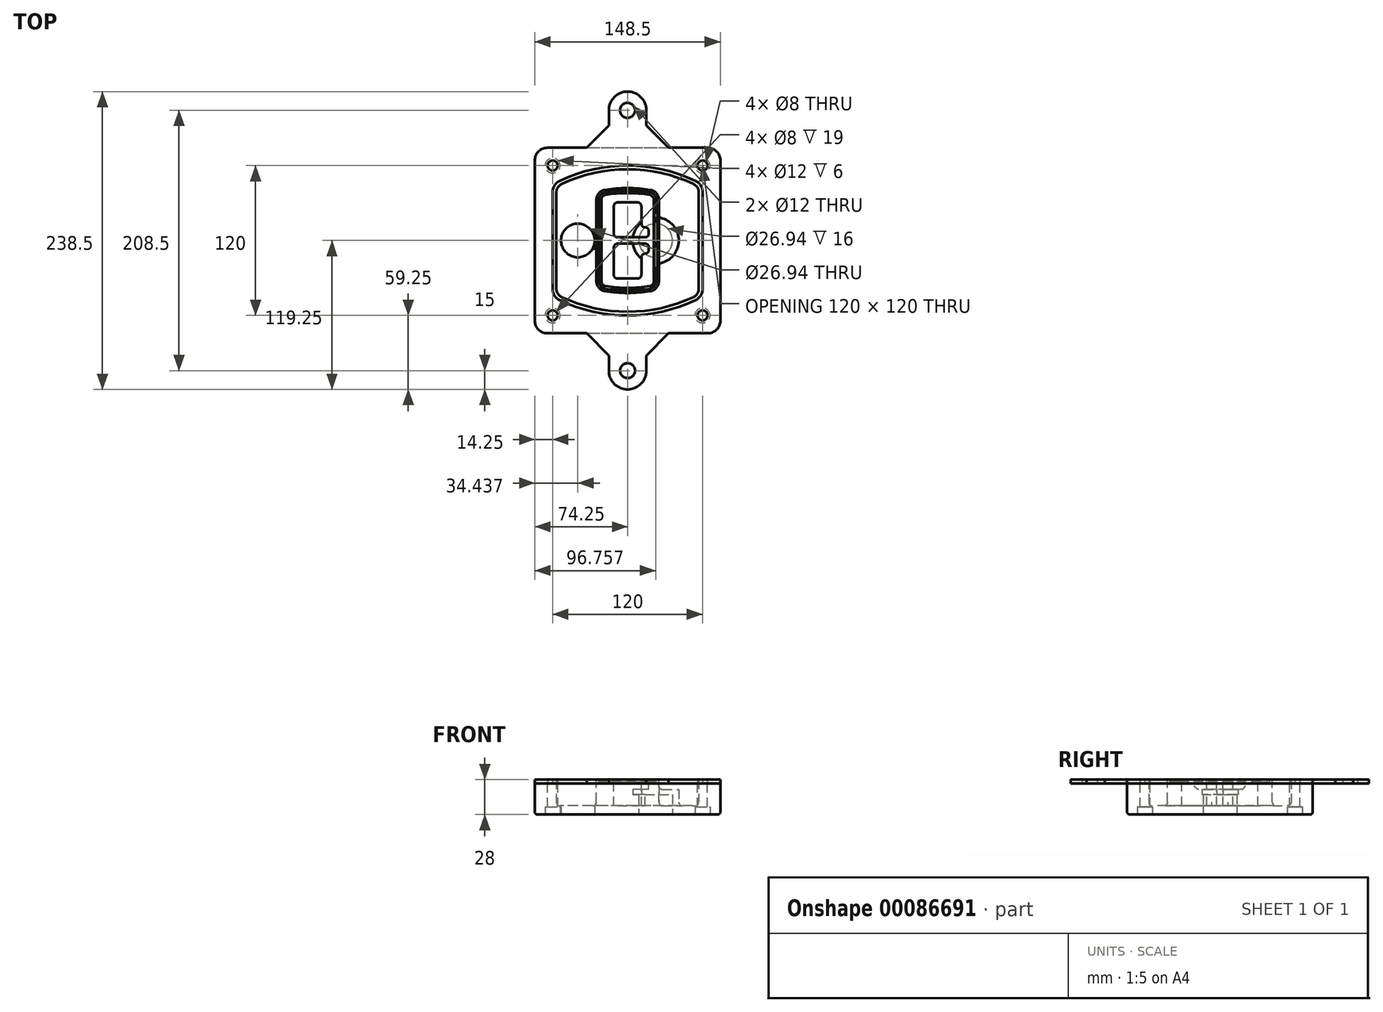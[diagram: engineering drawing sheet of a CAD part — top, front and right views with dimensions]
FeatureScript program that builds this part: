
annotation { "Feature Type Name" : "Feature", "Feature Type Description" : "" }
export const myFeature = defineFeature(function(context is Context, id is Id, definition is map)
    precondition{}
    {
        {
            var Q0;
            Q0=qCreatedBy(makeId("Top.planeOp"),FACE);
            var sketch = newSketch(context, id + "F0", { "sketchPlane" : qUnion([Q0])});
            skPoint(sketch, "E0.rect.middle", {"position": v(0, 0) * mm});
            skLineSegment(sketch, "E1.bottom", {"start": v(-64.25, -74.25) * mm, "end": v(64.25, -74.25) * mm});
            skLineSegment(sketch, "E1.top", {"start": v(-64.25, 74.25) * mm, "end": v(64.25, 74.25) * mm});
            skLineSegment(sketch, "E1.left", {"start": v(-74.25, -64.25) * mm, "end": v(-74.25, 64.25) * mm});
            skLineSegment(sketch, "E1.right", {"start": v(74.25, -64.25) * mm, "end": v(74.25, 64.25) * mm});
            skLineSegment(sketch, "E2", {"start": v(-74.25, 74.25) * mm, "end": v(74.25, -74.25) * mm, "construction": true});
            skLineSegment(sketch, "E3", {"start": v(74.25, 74.25) * mm, "end": v(-74.25, -74.25) * mm, "construction": true});
            skCircle(sketch, "E4", {"center": v(-60, 60) * mm, "radius": 4 * mm});
            skCircle(sketch, "E5", {"center": v(60, 60) * mm, "radius": 4 * mm});
            skCircle(sketch, "E6", {"center": v(60, -60) * mm, "radius": 4 * mm});
            skCircle(sketch, "E7", {"center": v(-60, -60) * mm, "radius": 4 * mm});
            skLineSegment(sketch, "E8", {"start": v(-60, 60) * mm, "end": v(60, 60) * mm, "construction": true});
            skLineSegment(sketch, "E9", {"start": v(60, 60) * mm, "end": v(60, -60) * mm, "construction": true});
            skLineSegment(sketch, "E10", {"start": v(60, -60) * mm, "end": v(-60, -60) * mm, "construction": true});
            skLineSegment(sketch, "E11", {"start": v(-60, -60) * mm, "end": v(-60, 60) * mm, "construction": true});
            skLineSegment(sketch, "E12", {"start": v(-60, 38.83) * mm, "end": v(-60, -38.83) * mm});
            skLineSegment(sketch, "E13", {"start": v(60, 38.83) * mm, "end": v(60, -38.83) * mm});
            skArc(sketch, "E14", {"start": v(54.26, 47.88) * mm, "mid": v(0, 60) * mm, "end": v(-54.26, 47.88) * mm});
            skArc(sketch, "E15", {"start": v(-54.26, -47.88) * mm, "mid": v(0, -60) * mm, "end": v(54.26, -47.88) * mm});
            skLineSegment(sketch, "E16", {"start": v(-60, 0) * mm, "end": v(60, 0) * mm, "construction": true});
            skPoint(sketch, "E17.visualSharp", {"position": v(-60, -45) * mm});
            skArc(sketch, "E17.filletArc", {"start": v(-60, -38.83) * mm, "mid": v(-58.44, -44.2) * mm, "end": v(-54.26, -47.88) * mm});
            skPoint(sketch, "E18.visualSharp", {"position": v(-60, 45) * mm});
            skArc(sketch, "E18.filletArc", {"start": v(-54.26, 47.88) * mm, "mid": v(-58.44, 44.2) * mm, "end": v(-60, 38.83) * mm});
            skPoint(sketch, "E19.visualSharp", {"position": v(60, 45) * mm});
            skArc(sketch, "E19.filletArc", {"start": v(60, 38.83) * mm, "mid": v(58.44, 44.2) * mm, "end": v(54.26, 47.88) * mm});
            skPoint(sketch, "E20.visualSharp", {"position": v(60, -45) * mm});
            skArc(sketch, "E20.filletArc", {"start": v(54.26, -47.88) * mm, "mid": v(58.44, -44.2) * mm, "end": v(60, -38.83) * mm});
            skPoint(sketch, "E21.visualSharp", {"position": v(-74.25, 74.25) * mm});
            skArc(sketch, "E21.filletArc", {"start": v(-64.25, 74.25) * mm, "mid": v(-71.32, 71.32) * mm, "end": v(-74.25, 64.25) * mm});
            skPoint(sketch, "E22.visualSharp", {"position": v(74.25, 74.25) * mm});
            skArc(sketch, "E22.filletArc", {"start": v(74.25, 64.25) * mm, "mid": v(71.32, 71.32) * mm, "end": v(64.25, 74.25) * mm});
            skPoint(sketch, "E23.visualSharp", {"position": v(74.25, -74.25) * mm});
            skArc(sketch, "E23.filletArc", {"start": v(64.25, -74.25) * mm, "mid": v(71.32, -71.32) * mm, "end": v(74.25, -64.25) * mm});
            skPoint(sketch, "E24.visualSharp", {"position": v(-74.25, -74.25) * mm});
            skArc(sketch, "E24.filletArc", {"start": v(-74.25, -64.25) * mm, "mid": v(-71.32, -71.32) * mm, "end": v(-64.25, -74.25) * mm});
            skArc(sketch, "E25.0", {"start": v(57, 38.83) * mm, "mid": v(55.9, 42.58) * mm, "end": v(52.98, 45.17) * mm});
            skLineSegment(sketch, "E25.1", {"start": v(57, 38.83) * mm, "end": v(57, -38.83) * mm});
            skArc(sketch, "E25.2", {"start": v(52.98, -45.17) * mm, "mid": v(55.9, -42.58) * mm, "end": v(57, -38.83) * mm});
            skArc(sketch, "E25.3", {"start": v(-52.98, -45.17) * mm, "mid": v(0, -57) * mm, "end": v(52.98, -45.17) * mm});
            skArc(sketch, "E25.4", {"start": v(-57, -38.83) * mm, "mid": v(-55.9, -42.58) * mm, "end": v(-52.98, -45.17) * mm});
            skArc(sketch, "E25.5", {"start": v(52.98, 45.17) * mm, "mid": v(0, 57) * mm, "end": v(-52.98, 45.17) * mm});
            skLineSegment(sketch, "E25.6", {"start": v(-57, 38.83) * mm, "end": v(-57, -38.83) * mm});
            skArc(sketch, "E25.7", {"start": v(-52.98, 45.17) * mm, "mid": v(-55.9, 42.58) * mm, "end": v(-57, 38.83) * mm});
            skArc(sketch, "E26.0", {"start": v(-55.96, 51.5) * mm, "mid": v(-61.82, 46.33) * mm, "end": v(-64, 38.83) * mm});
            skArc(sketch, "E26.1", {"start": v(55.96, 51.5) * mm, "mid": v(0, 64) * mm, "end": v(-55.96, 51.5) * mm});
            skArc(sketch, "E26.2", {"start": v(64, 38.83) * mm, "mid": v(61.82, 46.33) * mm, "end": v(55.96, 51.5) * mm});
            skLineSegment(sketch, "E26.3", {"start": v(64, 38.83) * mm, "end": v(64, -38.83) * mm});
            skArc(sketch, "E26.4", {"start": v(55.96, -51.5) * mm, "mid": v(61.82, -46.33) * mm, "end": v(64, -38.83) * mm});
            skLineSegment(sketch, "E26.5", {"start": v(-64, 38.83) * mm, "end": v(-64, -38.83) * mm});
            skArc(sketch, "E26.6", {"start": v(-55.96, -51.5) * mm, "mid": v(0, -64) * mm, "end": v(55.96, -51.5) * mm});
            skArc(sketch, "E26.7", {"start": v(-64, -38.83) * mm, "mid": v(-61.82, -46.33) * mm, "end": v(-55.96, -51.5) * mm});
            skSolve(sketch);
        }
        {
            var Q0;
            Q0=makeQuery(id+"F0.imprint","IMPRINT",FACE,{"disambiguationData":[TD([[makeQuery(id+"F0.imprint","IMPRINT",EDGE,{"derivedFrom":sQuery(id+"F0.wireOp",EDGE,"E1.bottom")}),1.0]])]});
            var Q1;
            Q1=makeQuery(id+"F0.imprint","IMPRINT",FACE,{"disambiguationData":[TD([[makeQuery(id+"F0.imprint","IMPRINT",EDGE,{"derivedFrom":sQuery(id+"F0.wireOp",EDGE,"E12")}),1.0]])]});
            var Q2;
            Q2=makeQuery(id+"F0.imprint","IMPRINT",FACE,{"disambiguationData":[TD([[makeQuery(id+"F0.imprint","IMPRINT",EDGE,{"derivedFrom":sQuery(id+"F0.wireOp",EDGE,"E25.0")}),1.0]])]});
            var Q3;
            Q3=makeQuery(id+"F0.imprint","IMPRINT",FACE,{"disambiguationData":[TD([[makeQuery(id+"F0.imprint","IMPRINT",EDGE,{"derivedFrom":sQuery(id+"F0.wireOp",EDGE,"E12")}),-1.0]])]});
            extrude(context, id + "F1", {"entities" : qUnion([Q0, Q1, Q2, Q3]), "oppositeDirection" : true, "depth" : 25 * mm});
        }
        {
            var Q0;
            Q0=makeQuery(id+"F0.imprint","IMPRINT",FACE,{"disambiguationData":[TD([[makeQuery(id+"F0.imprint","IMPRINT",EDGE,{"derivedFrom":sQuery(id+"F0.wireOp",EDGE,"E12")}),1.0]])]});
            extrude(context, id + "F2", {"entities" : qUnion([Q0]), "operationType" : NewBodyOperationType.ADD, "depth" : 3 * mm});
        }
        {
            var Q0;
            Q0=makeQuery(id+"F0.imprint","IMPRINT",FACE,{"disambiguationData":[TD([[makeQuery(id+"F0.imprint","IMPRINT",EDGE,{"derivedFrom":sQuery(id+"F0.wireOp",EDGE,"E25.0")}),1.0]])]});
            extrude(context, id + "F3", {"entities" : qUnion([Q0]), "operationType" : NewBodyOperationType.REMOVE, "oppositeDirection" : true, "depth" : 18 * mm});
        }
        {
            var Q0;
            Q0=makeQuery(id+"F2.opExtrude","CAP_FACE",FACE,{"disambiguationData":[OSD([sQuery(id+"F0.wireOp",EDGE,"E12"),sQuery(id+"F0.wireOp",EDGE,"E13"),sQuery(id+"F0.wireOp",EDGE,"E14"),sQuery(id+"F0.wireOp",EDGE,"E15"),sQuery(id+"F0.wireOp",EDGE,"E17.filletArc"),sQuery(id+"F0.wireOp",EDGE,"E18.filletArc"),sQuery(id+"F0.wireOp",EDGE,"E19.filletArc"),sQuery(id+"F0.wireOp",EDGE,"E20.filletArc"),sQuery(id+"F0.wireOp",EDGE,"E25.0"),sQuery(id+"F0.wireOp",EDGE,"E25.1"),sQuery(id+"F0.wireOp",EDGE,"E25.2"),sQuery(id+"F0.wireOp",EDGE,"E25.3"),sQuery(id+"F0.wireOp",EDGE,"E25.4"),sQuery(id+"F0.wireOp",EDGE,"E25.5"),sQuery(id+"F0.wireOp",EDGE,"E25.6"),sQuery(id+"F0.wireOp",EDGE,"E25.7")])],"isStart":false});
            var sketch = newSketch(context, id + "F4", { "sketchPlane" : qUnion([Q0])});
            skArc(sketch, "E27.0", {"start": v(-18.34, -40.45) * mm, "mid": v(0, -42) * mm, "end": v(18.34, -40.45) * mm});
            skArc(sketch, "E28.0", {"start": v(18.34, 40.45) * mm, "mid": v(0, 42) * mm, "end": v(-18.34, 40.45) * mm});
            skLineSegment(sketch, "E29", {"start": v(-25, 32.57) * mm, "end": v(-25, -32.57) * mm});
            skLineSegment(sketch, "E30", {"start": v(25, 32.57) * mm, "end": v(25, -32.57) * mm});
            skLineSegment(sketch, "E31", {"start": v(-25, 39.1) * mm, "end": v(25, 39.1) * mm, "construction": true});
            skLineSegment(sketch, "E32", {"start": v(-25, -39.1) * mm, "end": v(25, -39.1) * mm, "construction": true});
            skPoint(sketch, "E33.visualSharp", {"position": v(-25, 39.1) * mm});
            skArc(sketch, "E33.filletArc", {"start": v(-18.34, 40.45) * mm, "mid": v(-23.11, 37.73) * mm, "end": v(-25, 32.57) * mm});
            skPoint(sketch, "E34.visualSharp", {"position": v(25, 39.1) * mm});
            skArc(sketch, "E34.filletArc", {"start": v(25, 32.57) * mm, "mid": v(23.11, 37.73) * mm, "end": v(18.34, 40.45) * mm});
            skPoint(sketch, "E35.visualSharp", {"position": v(25, -39.1) * mm});
            skArc(sketch, "E35.filletArc", {"start": v(18.34, -40.45) * mm, "mid": v(23.11, -37.73) * mm, "end": v(25, -32.57) * mm});
            skPoint(sketch, "E36.visualSharp", {"position": v(-25, -39.1) * mm});
            skArc(sketch, "E36.filletArc", {"start": v(-25, -32.57) * mm, "mid": v(-23.11, -37.73) * mm, "end": v(-18.34, -40.45) * mm});
            skArc(sketch, "E37.0", {"start": v(52.98, 45.17) * mm, "mid": v(0, 57) * mm, "end": v(-52.98, 45.17) * mm});
            skArc(sketch, "E37.1", {"start": v(-52.98, 45.17) * mm, "mid": v(-55.9, 42.58) * mm, "end": v(-57, 38.83) * mm});
            skLineSegment(sketch, "E37.2", {"start": v(-57, 38.83) * mm, "end": v(-57, -38.83) * mm});
            skArc(sketch, "E37.3", {"start": v(-57, -38.83) * mm, "mid": v(-55.9, -42.58) * mm, "end": v(-52.98, -45.17) * mm});
            skArc(sketch, "E37.4", {"start": v(-52.98, -45.17) * mm, "mid": v(0, -57) * mm, "end": v(52.98, -45.17) * mm});
            skArc(sketch, "E37.5", {"start": v(52.98, -45.17) * mm, "mid": v(55.9, -42.58) * mm, "end": v(57, -38.83) * mm});
            skLineSegment(sketch, "E37.6", {"start": v(57, 38.83) * mm, "end": v(57, -38.83) * mm});
            skArc(sketch, "E37.7", {"start": v(57, 38.83) * mm, "mid": v(55.9, 42.58) * mm, "end": v(52.98, 45.17) * mm});
            skLineSegment(sketch, "E38.0", {"start": v(23, 32.57) * mm, "end": v(23, -32.57) * mm});
            skArc(sketch, "E38.1", {"start": v(18, -38.48) * mm, "mid": v(21.58, -36.44) * mm, "end": v(23, -32.57) * mm});
            skArc(sketch, "E38.2", {"start": v(-18, -38.48) * mm, "mid": v(0, -40) * mm, "end": v(18, -38.48) * mm});
            skArc(sketch, "E38.3", {"start": v(-23, -32.57) * mm, "mid": v(-21.58, -36.44) * mm, "end": v(-18, -38.48) * mm});
            skLineSegment(sketch, "E38.4", {"start": v(-23, 32.57) * mm, "end": v(-23, -32.57) * mm});
            skArc(sketch, "E38.5", {"start": v(23, 32.57) * mm, "mid": v(21.58, 36.44) * mm, "end": v(18, 38.48) * mm});
            skArc(sketch, "E38.6", {"start": v(-18, 38.48) * mm, "mid": v(-21.58, 36.44) * mm, "end": v(-23, 32.57) * mm});
            skArc(sketch, "E38.7", {"start": v(18, 38.48) * mm, "mid": v(0, 40) * mm, "end": v(-18, 38.48) * mm});
            skArc(sketch, "E39.0", {"start": v(21, 32.57) * mm, "mid": v(20.06, 35.15) * mm, "end": v(17.67, 36.5) * mm});
            skLineSegment(sketch, "E39.1", {"start": v(21, 32.57) * mm, "end": v(21, -32.57) * mm});
            skArc(sketch, "E39.2", {"start": v(17.67, -36.5) * mm, "mid": v(20.06, -35.15) * mm, "end": v(21, -32.57) * mm});
            skArc(sketch, "E39.3", {"start": v(-17.67, -36.5) * mm, "mid": v(0, -38) * mm, "end": v(17.67, -36.5) * mm});
            skArc(sketch, "E39.4", {"start": v(-21, -32.57) * mm, "mid": v(-20.06, -35.15) * mm, "end": v(-17.67, -36.5) * mm});
            skArc(sketch, "E39.5", {"start": v(17.67, 36.5) * mm, "mid": v(0, 38) * mm, "end": v(-17.67, 36.5) * mm});
            skLineSegment(sketch, "E39.6", {"start": v(-21, 32.57) * mm, "end": v(-21, -32.57) * mm});
            skArc(sketch, "E39.7", {"start": v(-17.67, 36.5) * mm, "mid": v(-20.06, 35.15) * mm, "end": v(-21, 32.57) * mm});
            skLineSegment(sketch, "E40", {"start": v(-25, 0) * mm, "end": v(25, 0) * mm, "construction": true});
            skLineSegment(sketch, "E41", {"start": v(-11, 5.5) * mm, "end": v(-11, 27.5) * mm});
            skLineSegment(sketch, "E42", {"start": v(-8, 30.5) * mm, "end": v(8, 30.5) * mm});
            skLineSegment(sketch, "E43", {"start": v(11, 27.5) * mm, "end": v(11, 13.5) * mm});
            skLineSegment(sketch, "E44", {"start": v(14, 10.5) * mm, "end": v(14, 10.5) * mm});
            skLineSegment(sketch, "E45", {"start": v(17, 7.5) * mm, "end": v(17, 5.5) * mm});
            skLineSegment(sketch, "E46", {"start": v(14, 2.5) * mm, "end": v(-8, 2.5) * mm});
            skPoint(sketch, "E47.visualSharp", {"position": v(-11, 30.5) * mm});
            skArc(sketch, "E47.filletArc", {"start": v(-8, 30.5) * mm, "mid": v(-10.12, 29.62) * mm, "end": v(-11, 27.5) * mm});
            skPoint(sketch, "E48.visualSharp", {"position": v(11, 30.5) * mm});
            skArc(sketch, "E48.filletArc", {"start": v(11, 27.5) * mm, "mid": v(10.12, 29.62) * mm, "end": v(8, 30.5) * mm});
            skPoint(sketch, "E49.visualSharp", {"position": v(11, 10.5) * mm});
            skArc(sketch, "E49.filletArc", {"start": v(11, 13.5) * mm, "mid": v(11.88, 11.38) * mm, "end": v(14, 10.5) * mm});
            skPoint(sketch, "E50.visualSharp", {"position": v(17, 10.5) * mm});
            skArc(sketch, "E50.filletArc", {"start": v(17, 7.5) * mm, "mid": v(16.12, 9.62) * mm, "end": v(14, 10.5) * mm});
            skPoint(sketch, "E51.visualSharp", {"position": v(17, 2.5) * mm});
            skArc(sketch, "E51.filletArc", {"start": v(14, 2.5) * mm, "mid": v(16.12, 3.38) * mm, "end": v(17, 5.5) * mm});
            skPoint(sketch, "E52.visualSharp", {"position": v(-11, 2.5) * mm});
            skArc(sketch, "E52.filletArc", {"start": v(-11, 5.5) * mm, "mid": v(-10.12, 3.38) * mm, "end": v(-8, 2.5) * mm});
            skLineSegment(sketch, "E53.0.MirrorCS", {"start": v(14, -2.5) * mm, "end": v(-8, -2.5) * mm});
            skArc(sketch, "E54.0.MirrorCS", {"start": v(-11, -5.5) * mm, "mid": v(-10.12, -3.38) * mm, "end": v(-8, -2.5) * mm});
            skLineSegment(sketch, "E55.0.MirrorCS", {"start": v(-11, -5.5) * mm, "end": v(-11, -27.5) * mm});
            skArc(sketch, "E56.0.MirrorCS", {"start": v(-8, -30.5) * mm, "mid": v(-10.12, -29.62) * mm, "end": v(-11, -27.5) * mm});
            skLineSegment(sketch, "E57.0.MirrorCS", {"start": v(-8, -30.5) * mm, "end": v(8, -30.5) * mm});
            skArc(sketch, "E58.0.MirrorCS", {"start": v(11, -27.5) * mm, "mid": v(10.12, -29.62) * mm, "end": v(8, -30.5) * mm});
            skLineSegment(sketch, "E59.0.MirrorCS", {"start": v(11, -27.5) * mm, "end": v(11, -13.5) * mm});
            skArc(sketch, "E60.0.MirrorCS", {"start": v(11, -13.5) * mm, "mid": v(11.88, -11.38) * mm, "end": v(14, -10.5) * mm});
            skArc(sketch, "E61.0.MirrorCS", {"start": v(17, -7.5) * mm, "mid": v(16.12, -9.62) * mm, "end": v(14, -10.5) * mm});
            skLineSegment(sketch, "E62.0.MirrorCS", {"start": v(17, -7.5) * mm, "end": v(17, -5.5) * mm});
            skArc(sketch, "E63.0.MirrorCS", {"start": v(14, -2.5) * mm, "mid": v(16.12, -3.38) * mm, "end": v(17, -5.5) * mm});
            skSolve(sketch);
        }
        {
            var Q0;
            Q0=makeQuery(id+"F4.imprint","IMPRINT",FACE,{"disambiguationData":[TD([[makeQuery(id+"F4.imprint","IMPRINT",EDGE,{"derivedFrom":sQuery(id+"F4.wireOp",EDGE,"E27.0")}),1.0]])]});
            var Q1;
            Q1=makeQuery(id+"F4.imprint","IMPRINT",FACE,{"disambiguationData":[TD([[makeQuery(id+"F4.imprint","IMPRINT",EDGE,{"derivedFrom":sQuery(id+"F4.wireOp",EDGE,"E38.0")}),-1.0]])]});
            var Q2;
            Q2=makeQuery(id+"F4.imprint","IMPRINT",FACE,{"disambiguationData":[TD([[makeQuery(id+"F4.imprint","IMPRINT",EDGE,{"derivedFrom":sQuery(id+"F4.wireOp",EDGE,"E39.0")}),1.0]])]});
            extrude(context, id + "F5", {"entities" : qUnion([Q0, Q1, Q2]), "operationType" : NewBodyOperationType.ADD, "endBound" : BoundingType.UP_TO_NEXT, "oppositeDirection" : true, "depth" : 25 * mm});
        }
        {
            var Q0;
            Q0=makeQuery(id+"F4.imprint","IMPRINT",FACE,{"disambiguationData":[TD([[makeQuery(id+"F4.imprint","IMPRINT",EDGE,{"derivedFrom":sQuery(id+"F4.wireOp",EDGE,"E38.0")}),-1.0]])]});
            extrude(context, id + "F6", {"entities" : qUnion([Q0]), "operationType" : NewBodyOperationType.REMOVE, "oppositeDirection" : true, "depth" : 2 * mm});
        }
        {
            var Q0;
            Q0=makeQuery(id+"F1.opExtrude","CAP_FACE",FACE,{"disambiguationData":[OSD([sQuery(id+"F0.wireOp",EDGE,"E1.bottom"),sQuery(id+"F0.wireOp",EDGE,"E1.top"),sQuery(id+"F0.wireOp",EDGE,"E1.left"),sQuery(id+"F0.wireOp",EDGE,"E1.right"),sQuery(id+"F0.wireOp",EDGE,"E4"),sQuery(id+"F0.wireOp",EDGE,"E5"),sQuery(id+"F0.wireOp",EDGE,"E6"),sQuery(id+"F0.wireOp",EDGE,"E7"),sQuery(id+"F0.wireOp",EDGE,"E21.filletArc"),sQuery(id+"F0.wireOp",EDGE,"E22.filletArc"),sQuery(id+"F0.wireOp",EDGE,"E23.filletArc"),sQuery(id+"F0.wireOp",EDGE,"E24.filletArc")])],"isStart":false});
            var sketch = newSketch(context, id + "F7", { "sketchPlane" : qUnion([Q0])});
            skCircle(sketch, "E64", {"center": v(22.5, 0) * mm, "radius": 13.47 * mm});
            skCircle(sketch, "E65", {"center": v(-39.81, 0) * mm, "radius": 13.47 * mm});
            skLineSegment(sketch, "E66", {"start": v(74.25, 0) * mm, "end": v(-74.25, 0) * mm});
            skCircle(sketch, "E67", {"center": v(22.5, 0) * mm, "radius": 18.47 * mm});
            skCircle(sketch, "E68", {"center": v(60, -60) * mm, "radius": 6 * mm});
            skCircle(sketch, "E69", {"center": v(-60, -60) * mm, "radius": 6 * mm});
            skCircle(sketch, "E70", {"center": v(-60, 60) * mm, "radius": 6 * mm});
            skCircle(sketch, "E71", {"center": v(60, 60) * mm, "radius": 6 * mm});
            skSolve(sketch);
        }
        {
            var Q0;
            {var subQ1=sQuery(id+"F7.wireOp",EDGE,"E66");var subQ4=sQuery(id+"F7.wireOp",EDGE,"E64");var subQ6=makeQuery(id+"F7.imprint","INTERSECT",VERTEX,{"disambiguationData":[OD(0.0)],"derivedFrom":[subQ4,subQ1]});Q0=makeQuery(id+"F7.imprint","IMPRINT",FACE,{"disambiguationData":[TD([[makeQuery(id+"F7.imprint","IMPRINT",EDGE,{"disambiguationData":[TD([[subQ6,-1.0]])],"derivedFrom":subQ4}),-1.0]])]});}
            var Q1;
            {var subQ0=sQuery(id+"F7.wireOp",EDGE,"E66");var subQ1=sQuery(id+"F7.wireOp",EDGE,"E64");var subQ3=makeQuery(id+"F7.imprint","INTERSECT",VERTEX,{"disambiguationData":[OD(0.0)],"derivedFrom":[subQ1,subQ0]});Q1=makeQuery(id+"F7.imprint","IMPRINT",FACE,{"disambiguationData":[TD([[makeQuery(id+"F7.imprint","IMPRINT",EDGE,{"disambiguationData":[TD([[subQ3,-1.0]])],"derivedFrom":subQ1}),1.0]])]});}
            var Q2;
            {var subQ0=sQuery(id+"F7.wireOp",EDGE,"E66");var subQ1=sQuery(id+"F7.wireOp",EDGE,"E64");var subQ3=makeQuery(id+"F7.imprint","INTERSECT",VERTEX,{"disambiguationData":[OD(0.0)],"derivedFrom":[subQ1,subQ0]});Q2=makeQuery(id+"F7.imprint","IMPRINT",FACE,{"disambiguationData":[TD([[makeQuery(id+"F7.imprint","IMPRINT",EDGE,{"disambiguationData":[TD([[subQ3,1.0]])],"derivedFrom":subQ1}),1.0]])]});}
            var Q3;
            {var subQ1=sQuery(id+"F7.wireOp",EDGE,"E66");var subQ4=sQuery(id+"F7.wireOp",EDGE,"E64");var subQ6=makeQuery(id+"F7.imprint","INTERSECT",VERTEX,{"disambiguationData":[OD(0.0)],"derivedFrom":[subQ4,subQ1]});Q3=makeQuery(id+"F7.imprint","IMPRINT",FACE,{"disambiguationData":[TD([[makeQuery(id+"F7.imprint","IMPRINT",EDGE,{"disambiguationData":[TD([[subQ6,1.0]])],"derivedFrom":subQ4}),-1.0]])]});}
            extrude(context, id + "F8", {"entities" : qUnion([Q0, Q1, Q2, Q3]), "operationType" : NewBodyOperationType.ADD, "oppositeDirection" : true, "depth" : 20 * mm});
        }
        {
            var Q0;
            {var subQ0=sQuery(id+"F7.wireOp",EDGE,"E66");var subQ1=sQuery(id+"F7.wireOp",EDGE,"E64");var subQ3=makeQuery(id+"F7.imprint","INTERSECT",VERTEX,{"disambiguationData":[OD(0.0)],"derivedFrom":[subQ1,subQ0]});Q0=makeQuery(id+"F7.imprint","IMPRINT",FACE,{"disambiguationData":[TD([[makeQuery(id+"F7.imprint","IMPRINT",EDGE,{"disambiguationData":[TD([[subQ3,-1.0]])],"derivedFrom":subQ1}),1.0]])]});}
            var Q1;
            {var subQ0=sQuery(id+"F7.wireOp",EDGE,"E66");var subQ1=sQuery(id+"F7.wireOp",EDGE,"E64");var subQ3=makeQuery(id+"F7.imprint","INTERSECT",VERTEX,{"disambiguationData":[OD(0.0)],"derivedFrom":[subQ1,subQ0]});Q1=makeQuery(id+"F7.imprint","IMPRINT",FACE,{"disambiguationData":[TD([[makeQuery(id+"F7.imprint","IMPRINT",EDGE,{"disambiguationData":[TD([[subQ3,1.0]])],"derivedFrom":subQ1}),1.0]])]});}
            extrude(context, id + "F9", {"entities" : qUnion([Q0, Q1]), "operationType" : NewBodyOperationType.REMOVE, "oppositeDirection" : true, "depth" : 16 * mm});
        }
        {
            var Q0;
            {var subQ0=sQuery(id+"F7.wireOp",EDGE,"E66");var subQ1=sQuery(id+"F7.wireOp",EDGE,"E65");var subQ3=makeQuery(id+"F7.imprint","INTERSECT",VERTEX,{"disambiguationData":[OD(0.0)],"derivedFrom":[subQ1,subQ0]});Q0=makeQuery(id+"F7.imprint","IMPRINT",FACE,{"disambiguationData":[TD([[makeQuery(id+"F7.imprint","IMPRINT",EDGE,{"disambiguationData":[TD([[subQ3,-1.0]])],"derivedFrom":subQ1}),1.0]])]});}
            var Q1;
            {var subQ0=sQuery(id+"F7.wireOp",EDGE,"E66");var subQ1=sQuery(id+"F7.wireOp",EDGE,"E65");var subQ3=makeQuery(id+"F7.imprint","INTERSECT",VERTEX,{"disambiguationData":[OD(0.0)],"derivedFrom":[subQ1,subQ0]});Q1=makeQuery(id+"F7.imprint","IMPRINT",FACE,{"disambiguationData":[TD([[makeQuery(id+"F7.imprint","IMPRINT",EDGE,{"disambiguationData":[TD([[subQ3,1.0]])],"derivedFrom":subQ1}),1.0]])]});}
            extrude(context, id + "F10", {"entities" : qUnion([Q0, Q1]), "operationType" : NewBodyOperationType.REMOVE, "oppositeDirection" : true, "depth" : 25 * mm});
        }
        {
            var Q0;
            Q0=makeQuery(id+"F7.imprint","IMPRINT",FACE,{"disambiguationData":[TD([[makeQuery(id+"F7.imprint","IMPRINT",EDGE,{"derivedFrom":sQuery(id+"F7.wireOp",EDGE,"E68")}),1.0]])]});
            var Q1;
            Q1=makeQuery(id+"F7.imprint","IMPRINT",FACE,{"disambiguationData":[TD([[makeQuery(id+"F7.imprint","IMPRINT",EDGE,{"derivedFrom":makeQuery(id+"F1.opExtrude","CAP_EDGE",EDGE,{"disambiguationData":[OSD([sQuery(id+"F0.wireOp",EDGE,"E5")])],"isStart":false})}),-1.0]])]});
            var Q2;
            Q2=makeQuery(id+"F7.imprint","IMPRINT",FACE,{"disambiguationData":[TD([[makeQuery(id+"F7.imprint","IMPRINT",EDGE,{"derivedFrom":sQuery(id+"F7.wireOp",EDGE,"E69")}),1.0]])]});
            var Q3;
            Q3=makeQuery(id+"F7.imprint","IMPRINT",FACE,{"disambiguationData":[TD([[makeQuery(id+"F7.imprint","IMPRINT",EDGE,{"derivedFrom":makeQuery(id+"F1.opExtrude","CAP_EDGE",EDGE,{"disambiguationData":[OSD([sQuery(id+"F0.wireOp",EDGE,"E4")])],"isStart":false})}),-1.0]])]});
            var Q4;
            Q4=makeQuery(id+"F7.imprint","IMPRINT",FACE,{"disambiguationData":[TD([[makeQuery(id+"F7.imprint","IMPRINT",EDGE,{"derivedFrom":sQuery(id+"F7.wireOp",EDGE,"E70")}),1.0]])]});
            var Q5;
            Q5=makeQuery(id+"F7.imprint","IMPRINT",FACE,{"disambiguationData":[TD([[makeQuery(id+"F7.imprint","IMPRINT",EDGE,{"derivedFrom":makeQuery(id+"F1.opExtrude","CAP_EDGE",EDGE,{"disambiguationData":[OSD([sQuery(id+"F0.wireOp",EDGE,"E7")])],"isStart":false})}),-1.0]])]});
            var Q6;
            Q6=makeQuery(id+"F7.imprint","IMPRINT",FACE,{"disambiguationData":[TD([[makeQuery(id+"F7.imprint","IMPRINT",EDGE,{"derivedFrom":sQuery(id+"F7.wireOp",EDGE,"E71")}),1.0]])]});
            var Q7;
            Q7=makeQuery(id+"F7.imprint","IMPRINT",FACE,{"disambiguationData":[TD([[makeQuery(id+"F7.imprint","IMPRINT",EDGE,{"derivedFrom":makeQuery(id+"F1.opExtrude","CAP_EDGE",EDGE,{"disambiguationData":[OSD([sQuery(id+"F0.wireOp",EDGE,"E6")])],"isStart":false})}),-1.0]])]});
            extrude(context, id + "F11", {"entities" : qUnion([Q0, Q1, Q2, Q3, Q4, Q5, Q6, Q7]), "operationType" : NewBodyOperationType.REMOVE, "oppositeDirection" : true, "depth" : 6 * mm});
        }
        {
            var Q0;
            Q0=makeQuery(id+"F9.boolean.opBoolean","COPY",FACE,{"derivedFrom":makeQuery(id+"F9.opExtrude","CAP_FACE",FACE,{"disambiguationData":[OSD([sQuery(id+"F7.wireOp",EDGE,"E64")])],"isStart":false})});
            var sketch = newSketch(context, id + "F12", { "sketchPlane" : qUnion([Q0])});
            skArc(sketch, "E72.0", {"start": v(11, 14.45) * mm, "mid": v(6.45, 9.13) * mm, "end": v(4.2, 2.5) * mm});
            skArc(sketch, "E72.1", {"start": v(4.2, -2.5) * mm, "mid": v(6.45, -9.13) * mm, "end": v(11, -14.45) * mm});
            skLineSegment(sketch, "E73", {"start": v(4.2, -2.5) * mm, "end": v(14, -2.5) * mm});
            skLineSegment(sketch, "E74.0", {"start": v(14, 2.5) * mm, "end": v(4.2, 2.5) * mm});
            skArc(sketch, "E74.1", {"start": v(14, 2.5) * mm, "mid": v(16.12, 3.38) * mm, "end": v(17, 5.5) * mm});
            skLineSegment(sketch, "E74.2", {"start": v(17, 7.5) * mm, "end": v(17, 5.5) * mm});
            skArc(sketch, "E74.3", {"start": v(17, 7.5) * mm, "mid": v(16.12, 9.62) * mm, "end": v(14, 10.5) * mm});
            skArc(sketch, "E74.4", {"start": v(11, 13.5) * mm, "mid": v(11.88, 11.38) * mm, "end": v(14, 10.5) * mm});
            skLineSegment(sketch, "E74.5", {"start": v(11, 14.45) * mm, "end": v(11, 13.5) * mm});
            skLineSegment(sketch, "E74.7", {"start": v(14, -2.5) * mm, "end": v(4.2, -2.5) * mm});
            skArc(sketch, "E74.8", {"start": v(14, -2.5) * mm, "mid": v(16.12, -3.38) * mm, "end": v(17, -5.5) * mm});
            skLineSegment(sketch, "E74.9", {"start": v(17, -7.5) * mm, "end": v(17, -5.5) * mm});
            skArc(sketch, "E74.10", {"start": v(17, -7.5) * mm, "mid": v(16.12, -9.62) * mm, "end": v(14, -10.5) * mm});
            skArc(sketch, "E74.11", {"start": v(11, -13.5) * mm, "mid": v(11.88, -11.38) * mm, "end": v(14, -10.5) * mm});
            skLineSegment(sketch, "E74.12", {"start": v(11, -14.45) * mm, "end": v(11, -13.5) * mm});
            skPoint(sketch, "E75.orphan", {"position": v(11, -27.5) * mm});
            skPoint(sketch, "E76.orphan", {"position": v(-8, -2.5) * mm});
            skPoint(sketch, "E77.orphan", {"position": v(-8, 2.5) * mm});
            skPoint(sketch, "E78.orphan", {"position": v(11, 27.5) * mm});
            skSolve(sketch);
        }
        {
            var Q0;
            {var subQ7=sQuery(id+"F12.wireOp",EDGE,"E72.0");var subQ14=sQuery(id+"F12.wireOp",EDGE,"E72.1");var subQ16=sQuery(id+"F12.wireOp",EDGE,"E74.1");var subQ18=sQuery(id+"F12.wireOp",EDGE,"E74.8");Q0=qUnion([makeQuery(id+"F12.imprint","IMPRINT",FACE,{"disambiguationData":[TD([[makeQuery(id+"F12.imprint","IMPRINT",EDGE,{"derivedFrom":subQ7}),1.0]])]}),makeQuery(id+"F12.imprint","IMPRINT",FACE,{"disambiguationData":[TD([[makeQuery(id+"F12.imprint","IMPRINT",EDGE,{"derivedFrom":subQ14}),1.0]])]}),makeQuery(id+"F12.imprint","IMPRINT",FACE,{"disambiguationData":[TD([[makeQuery(id+"F12.imprint","IMPRINT",EDGE,{"derivedFrom":subQ16}),1.0]])]}),makeQuery(id+"F12.imprint","IMPRINT",FACE,{"disambiguationData":[TD([[makeQuery(id+"F12.imprint","IMPRINT",EDGE,{"derivedFrom":subQ18}),-1.0]])]})]);}
            var Q1;
            Q1=makeQuery(id+"F5.boolean.opBoolean","SPLIT",FACE,{"disambiguationData":[TD([makeQuery(id+"F5.opExtrude","SWEPT_FACE",FACE,{"disambiguationData":[OSD([sQuery(id+"F4.wireOp",EDGE,"E41")])]})])],"derivedFrom":makeQuery(id+"F3.boolean.opBoolean","COPY",FACE,{"derivedFrom":makeQuery(id+"F3.opExtrude","CAP_FACE",FACE,{"disambiguationData":[OSD([sQuery(id+"F0.wireOp",EDGE,"E25.0"),sQuery(id+"F0.wireOp",EDGE,"E25.1"),sQuery(id+"F0.wireOp",EDGE,"E25.2"),sQuery(id+"F0.wireOp",EDGE,"E25.3"),sQuery(id+"F0.wireOp",EDGE,"E25.4"),sQuery(id+"F0.wireOp",EDGE,"E25.5"),sQuery(id+"F0.wireOp",EDGE,"E25.6"),sQuery(id+"F0.wireOp",EDGE,"E25.7")])],"isStart":false})})});
            extrude(context, id + "F13", {"entities" : qUnion([Q0]), "operationType" : NewBodyOperationType.REMOVE, "endBound" : BoundingType.UP_TO_SURFACE, "endBoundEntityFace" : qUnion([Q1]), "depth" : 25 * mm});
        }
        {
            var Q0;
            Q0=makeQuery(id+"F3.boolean.opBoolean","COPY",EDGE,{"derivedFrom":makeQuery(id+"F3.opExtrude","CAP_EDGE",EDGE,{"disambiguationData":[OSD([sQuery(id+"F0.wireOp",EDGE,"E25.6")])],"isStart":false})});
            var Q1;
            Q1=makeQuery(id+"F8.boolean.opBoolean","INTERSECT",EDGE,{"derivedFrom":[makeQuery(id+"F5.opExtrude","SWEPT_FACE",FACE,{"disambiguationData":[OSD([sQuery(id+"F4.wireOp",EDGE,"E30")])]}),makeQuery(id+"F8.opExtrude","CAP_FACE",FACE,{"disambiguationData":[OSD([sQuery(id+"F7.wireOp",EDGE,"E67")])],"isStart":false})]});
            var Q2;
            Q2=makeQuery(id+"F8.boolean.opBoolean","INTERSECT",EDGE,{"disambiguationData":[OD(1.0)],"derivedFrom":[makeQuery(id+"F5.opExtrude","SWEPT_FACE",FACE,{"disambiguationData":[OSD([sQuery(id+"F4.wireOp",EDGE,"E30")])]}),makeQuery(id+"F8.opExtrude","SWEPT_FACE",FACE,{"disambiguationData":[OSD([sQuery(id+"F7.wireOp",EDGE,"E67")])]})]});
            var Q3;
            {var subQ0=sQuery(id+"F4.wireOp",EDGE,"E30");Q3=makeQuery(id+"F8.boolean.opBoolean","SPLIT",EDGE,{"disambiguationData":[TD([makeQuery(id+"F5.opExtrude","SWEPT_FACE",FACE,{"disambiguationData":[OSD([sQuery(id+"F4.wireOp",EDGE,"E35.filletArc")])]})])],"derivedFrom":makeQuery(id+"F5.opExtrude","CAP_EDGE",EDGE,{"disambiguationData":[OSD([subQ0])],"isStart":false})});}
            var Q4;
            {var subQ0=sQuery(id+"F0.wireOp",EDGE,"E25.7");var subQ1=sQuery(id+"F0.wireOp",EDGE,"E25.1");var subQ2=sQuery(id+"F0.wireOp",EDGE,"E25.6");var subQ3=sQuery(id+"F0.wireOp",EDGE,"E25.5");var subQ4=sQuery(id+"F0.wireOp",EDGE,"E25.4");var subQ5=sQuery(id+"F0.wireOp",EDGE,"E25.0");var subQ6=sQuery(id+"F0.wireOp",EDGE,"E25.2");var subQ7=sQuery(id+"F0.wireOp",EDGE,"E25.3");Q4=makeQuery(id+"F8.boolean.opBoolean","INTERSECT",EDGE,{"derivedFrom":[makeQuery(id+"F5.boolean.opBoolean","SPLIT",FACE,{"disambiguationData":[TD([makeQuery(id+"F2.opExtrude","SWEPT_FACE",FACE,{"disambiguationData":[OSD([subQ5])]})])],"derivedFrom":makeQuery(id+"F3.boolean.opBoolean","COPY",FACE,{"derivedFrom":makeQuery(id+"F3.opExtrude","CAP_FACE",FACE,{"disambiguationData":[OSD([subQ5,subQ1,subQ6,subQ7,subQ4,subQ3,subQ2,subQ0])],"isStart":false})})}),makeQuery(id+"F8.opExtrude","SWEPT_FACE",FACE,{"disambiguationData":[OSD([sQuery(id+"F7.wireOp",EDGE,"E67")])]})]});}
            var Q5;
            Q5=makeQuery(id+"F8.boolean.opBoolean","INTERSECT",EDGE,{"disambiguationData":[OD(0.0)],"derivedFrom":[makeQuery(id+"F5.opExtrude","SWEPT_FACE",FACE,{"disambiguationData":[OSD([sQuery(id+"F4.wireOp",EDGE,"E30")])]}),makeQuery(id+"F8.opExtrude","SWEPT_FACE",FACE,{"disambiguationData":[OSD([sQuery(id+"F7.wireOp",EDGE,"E67")])]})]});
            fillet(context, id + "F14", {"entities" : qUnion([Q0, Q1, Q2, Q3, Q4, Q5]), "radius" : 3 * mm, "tangentPropagation" : true, "allowEdgeOverflow" : false});
        }
        {
            var Q0;
            Q0=makeQuery(id+"F1.opExtrude","CAP_EDGE",EDGE,{"disambiguationData":[OSD([sQuery(id+"F0.wireOp",EDGE,"E1.bottom")])],"isStart":false});
            fillet(context, id + "F15", {"entities" : qUnion([Q0]), "radius" : 2 * mm, "tangentPropagation" : true, "allowEdgeOverflow" : false});
        }
        {
            var Q0;
            {var subQ0=sQuery(id+"F0.wireOp",EDGE,"E22.filletArc");var subQ1=sQuery(id+"F0.wireOp",EDGE,"E7");var subQ2=sQuery(id+"F0.wireOp",EDGE,"E6");var subQ3=sQuery(id+"F0.wireOp",EDGE,"E5");var subQ4=sQuery(id+"F0.wireOp",EDGE,"E4");var subQ5=sQuery(id+"F0.wireOp",EDGE,"E1.bottom");var subQ6=sQuery(id+"F0.wireOp",EDGE,"E21.filletArc");var subQ7=sQuery(id+"F0.wireOp",EDGE,"E1.top");var subQ8=sQuery(id+"F0.wireOp",EDGE,"E1.left");var subQ9=sQuery(id+"F0.wireOp",EDGE,"E1.right");var subQ10=sQuery(id+"F0.wireOp",EDGE,"E23.filletArc");var subQ11=sQuery(id+"F0.wireOp",EDGE,"E24.filletArc");Q0=makeQuery(id+"F2.boolean.opBoolean","SPLIT",FACE,{"disambiguationData":[TD([makeQuery(id+"F1.opExtrude","SWEPT_FACE",FACE,{"disambiguationData":[OSD([subQ5])]})])],"derivedFrom":makeQuery(id+"F1.opExtrude","CAP_FACE",FACE,{"disambiguationData":[OSD([subQ5,subQ7,subQ8,subQ9,subQ4,subQ3,subQ2,subQ1,subQ6,subQ0,subQ10,subQ11])],"isStart":true})});}
            var sketch = newSketch(context, id + "F16", { "sketchPlane" : qUnion([Q0])});
            skLineSegment(sketch, "E79", {"start": v(0, 74.25) * mm, "end": v(0, 104.25) * mm, "construction": true});
            skCircle(sketch, "E80", {"center": v(0, 104.25) * mm, "radius": 6 * mm});
            skArc(sketch, "E81", {"start": v(14.8, 106.7) * mm, "mid": v(0, 119.25) * mm, "end": v(-14.8, 106.7) * mm});
            skLineSegment(sketch, "E82", {"start": v(-14.8, 106.7) * mm, "end": v(-14.8, 92.25) * mm});
            skLineSegment(sketch, "E83", {"start": v(14.8, 106.7) * mm, "end": v(14.8, 92.25) * mm});
            skLineSegment(sketch, "E84", {"start": v(0, 0) * mm, "end": v(74.25, 0) * mm, "construction": true});
            skLineSegment(sketch, "E85", {"start": v(0, 0) * mm, "end": v(-74.25, 0) * mm, "construction": true});
            skLineSegment(sketch, "E86", {"start": v(-14.8, 92.25) * mm, "end": v(-32.8, 74.25) * mm});
            skLineSegment(sketch, "E87", {"start": v(14.8, 92.25) * mm, "end": v(32.8, 74.25) * mm});
            skLineSegment(sketch, "E88.0", {"start": v(64.25, 74.25) * mm, "end": v(-64.25, 74.25) * mm});
            skLineSegment(sketch, "E89.MirrorCS", {"start": v(-14.8, -92.25) * mm, "end": v(-32.8, -74.25) * mm});
            skLineSegment(sketch, "E90.MirrorCS", {"start": v(-14.8, -106.7) * mm, "end": v(-14.8, -92.25) * mm});
            skCircle(sketch, "E91.MirrorC", {"center": v(0, -104.25) * mm, "radius": 6 * mm});
            skArc(sketch, "E92.MirrorCS", {"start": v(14.8, -106.7) * mm, "mid": v(0, -119.25) * mm, "end": v(-14.8, -106.7) * mm});
            skLineSegment(sketch, "E93.MirrorCS", {"start": v(14.8, -92.25) * mm, "end": v(32.8, -74.25) * mm});
            skLineSegment(sketch, "E94.MirrorCS", {"start": v(14.8, -106.7) * mm, "end": v(14.8, -92.25) * mm});
            skSolve(sketch);
        }
        {
            var Q0;
            Q0=makeQuery(id+"F16.imprint","IMPRINT",FACE,{"disambiguationData":[TD([[makeQuery(id+"F16.imprint","IMPRINT",EDGE,{"derivedFrom":sQuery(id+"F16.wireOp",EDGE,"E80")}),-1.0]])]});
            var Q1;
            {var subQ0=sQuery(id+"F16.wireOp",EDGE,"E89.MirrorCS");Q1=makeQuery(id+"F16.imprint","IMPRINT",FACE,{"disambiguationData":[TD([[makeQuery(id+"F16.imprint","IMPRINT",EDGE,{"derivedFrom":subQ0}),-1.0]])]});}
            var Q2;
            Q2=makeQuery(id+"F16.imprint","IMPRINT",FACE,{"disambiguationData":[TD([[makeQuery(id+"F16.imprint","IMPRINT",EDGE,{"derivedFrom":makeQuery(id+"F1.opExtrude","CAP_EDGE",EDGE,{"disambiguationData":[OSD([sQuery(id+"F0.wireOp",EDGE,"E1.left")])],"isStart":true})}),-1.0]])]});
            var Q3;
            Q3=makeQuery(id+"F2.opExtrude","CAP_FACE",FACE,{"disambiguationData":[OSD([sQuery(id+"F0.wireOp",EDGE,"E12"),sQuery(id+"F0.wireOp",EDGE,"E13"),sQuery(id+"F0.wireOp",EDGE,"E14"),sQuery(id+"F0.wireOp",EDGE,"E15"),sQuery(id+"F0.wireOp",EDGE,"E17.filletArc"),sQuery(id+"F0.wireOp",EDGE,"E18.filletArc"),sQuery(id+"F0.wireOp",EDGE,"E19.filletArc"),sQuery(id+"F0.wireOp",EDGE,"E20.filletArc"),sQuery(id+"F0.wireOp",EDGE,"E25.0"),sQuery(id+"F0.wireOp",EDGE,"E25.1"),sQuery(id+"F0.wireOp",EDGE,"E25.2"),sQuery(id+"F0.wireOp",EDGE,"E25.3"),sQuery(id+"F0.wireOp",EDGE,"E25.4"),sQuery(id+"F0.wireOp",EDGE,"E25.5"),sQuery(id+"F0.wireOp",EDGE,"E25.6"),sQuery(id+"F0.wireOp",EDGE,"E25.7")])],"isStart":false});
            extrude(context, id + "F17", {"entities" : qUnion([Q0, Q1, Q2]), "endBound" : BoundingType.UP_TO_SURFACE, "endBoundEntityFace" : qUnion([Q3]), "depth" : 25 * mm});
        }
    });
